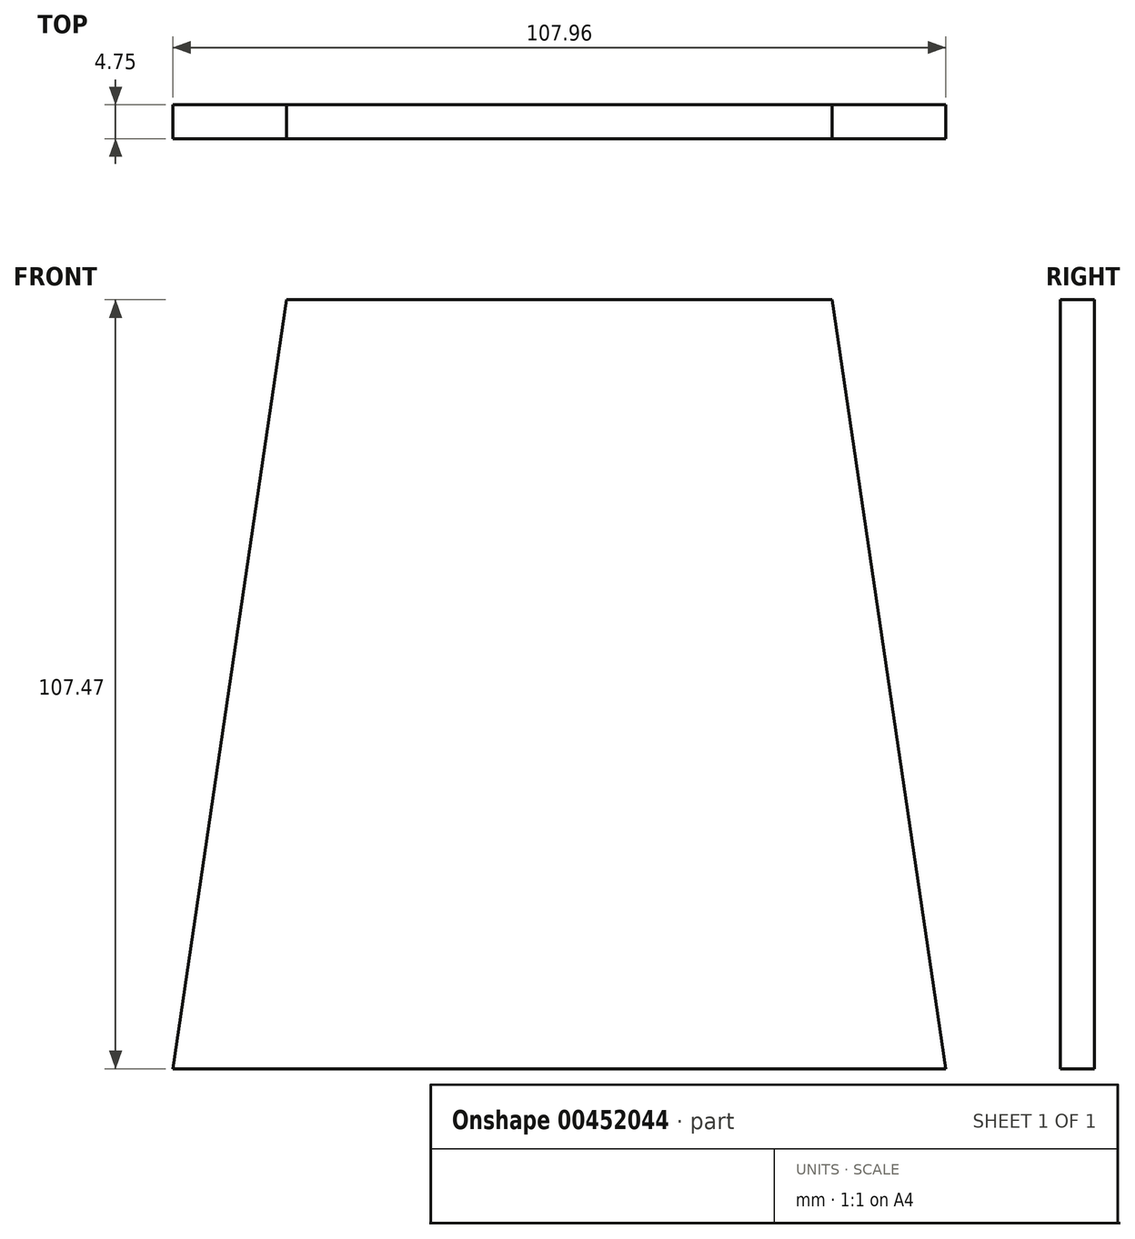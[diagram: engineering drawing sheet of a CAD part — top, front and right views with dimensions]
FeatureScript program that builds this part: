
annotation { "Feature Type Name" : "Feature", "Feature Type Description" : "" }
export const myFeature = defineFeature(function(context is Context, id is Id, definition is map)
    precondition{}
    {
        {
            var Q0;
            Q0=qCreatedBy(makeId("Front.planeOp"),FACE);
            var sketch = newSketch(context, id + "F0", { "sketchPlane" : qUnion([Q0])});
            skLineSegment(sketch, "E0", {"start": v(0, 0) * mm, "end": v(-38.1, 0) * mm});
            skLineSegment(sketch, "E1", {"start": v(0, -107.47) * mm, "end": v(-53.97, -107.47) * mm});
            skLineSegment(sketch, "E2", {"start": v(-38.1, 0) * mm, "end": v(-53.98, -107.47) * mm});
            skLineSegment(sketch, "E3.MirrorCS", {"start": v(38.1, 0) * mm, "end": v(53.98, -107.47) * mm});
            skLineSegment(sketch, "E4.MirrorCS", {"start": v(0, 0) * mm, "end": v(38.1, 0) * mm});
            skLineSegment(sketch, "E5.MirrorCS", {"start": v(0, -107.47) * mm, "end": v(53.97, -107.47) * mm});
            skSolve(sketch);
        }
        {
            var Q0;
            Q0=makeQuery(id+"F0.imprint","IMPRINT",FACE,{"disambiguationData":[TD([[makeQuery(id+"F0.imprint","IMPRINT",EDGE,{"derivedFrom":sQuery(id+"F0.wireOp",EDGE,"E0")}),1.0]])]});
            extrude(context, id + "F1", {"entities" : qUnion([Q0]), "depth" : 4.75 * mm});
        }
    });
